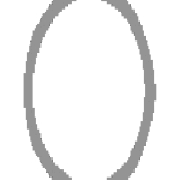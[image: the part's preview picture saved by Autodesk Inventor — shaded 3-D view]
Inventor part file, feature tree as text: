
AUTODESK INVENTOR PART (.ipt)
format: ipt  version: 2021 (Build 250183000, 183)  size: 112,640 bytes
history: native  units: in
note: dims shown in document units (in); Inventor stores cm internally (conversion verified against a paired STEP export)
features: other x4, sketch x3, plane x1
ambient origin geometry x8: Origin, YZ Plane, XZ Plane, XY Plane, X Axis, Y Axis, Z Axis, Center Point
bodies: Solid1 (feature_tree), Body (feature_tree)
feature tree (8):
  other  "Driven Length"
  other  "Frame Generator"
  other  "Start Plane"
  other  "End Plane"
  sketch  "Sketch"  dims[d2=19.6751in d4=-0.0in d5=19.6751in d6=0.12in d7=0.0in d8=90.0deg d9=19.6751in]
  sketch  "Sketch2"  dims[d0=1.0in]
  plane  "Work Plane3"
  sketch  "Sketch3"  dims[d1=0.065in]
